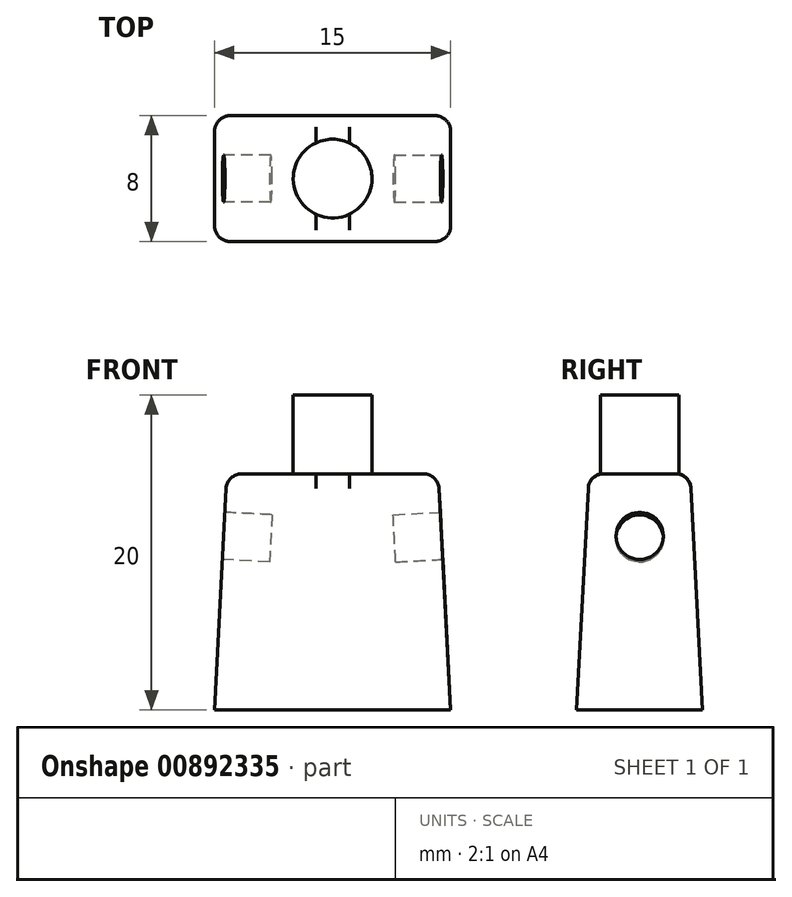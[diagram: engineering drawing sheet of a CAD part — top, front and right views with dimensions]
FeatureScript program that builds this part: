
annotation { "Feature Type Name" : "Feature", "Feature Type Description" : "" }
export const myFeature = defineFeature(function(context is Context, id is Id, definition is map)
    precondition{}
    {
        {
            var Q0;
            Q0=qCreatedBy(makeId("Top.planeOp"),FACE);
            var sketch = newSketch(context, id + "F0", { "sketchPlane" : qUnion([Q0])});
            skLineSegment(sketch, "E0.bottom", {"start": v(7.5, -4) * mm, "end": v(-7.5, -4) * mm});
            skLineSegment(sketch, "E0.top", {"start": v(7.5, 4) * mm, "end": v(-7.5, 4) * mm});
            skLineSegment(sketch, "E0.left", {"start": v(7.5, -4) * mm, "end": v(7.5, 4) * mm});
            skLineSegment(sketch, "E0.right", {"start": v(-7.5, -4) * mm, "end": v(-7.5, 4) * mm});
            skPoint(sketch, "E0.middle", {"position": v(0, 0) * mm});
            skSolve(sketch);
        }
        {
            var Q0;
            Q0 = qSketchRegion(id + "F0", true);
            extrude(context, id + "F1", {"entities" : qUnion([Q0]), "depth" : 15 * mm, "offsetDistance" : 25.4 * mm, "hasDraft" : true, "draftAngle" : 3 * degree, "draftPullDirection" : true});
        }
        {
            var Q0;
            Q0=makeQuery(id+"F1.opExtrude","CAP_FACE",FACE,{"disambiguationData":[OSD([sQuery(id+"F0.wireOp",EDGE,"E0.bottom"),sQuery(id+"F0.wireOp",EDGE,"E0.top"),sQuery(id+"F0.wireOp",EDGE,"E0.left"),sQuery(id+"F0.wireOp",EDGE,"E0.right")])],"isStart":false});
            var sketch = newSketch(context, id + "F2", { "sketchPlane" : qUnion([Q0])});
            skCircle(sketch, "E1", {"center": v(0, 0) * mm, "radius": 2.5 * mm});
            skSolve(sketch);
        }
        {
            var Q0;
            Q0 = qSketchRegion(id + "F2", true);
            extrude(context, id + "F3", {"entities" : qUnion([Q0]), "operationType" : NewBodyOperationType.ADD, "depth" : 5 * mm, "offsetDistance" : 25.4 * mm});
        }
        {
            var Q0;
            Q0=makeQuery(id+"F1.opExtrude","SWEPT_EDGE",EDGE,{"disambiguationData":[OSD([sQuery(id+"F0.wireOp",EDGE,"E0.bottom"),sQuery(id+"F0.wireOp",EDGE,"E0.left")])]});
            var Q1;
            Q1=makeQuery(id+"F1.opExtrude","SWEPT_EDGE",EDGE,{"disambiguationData":[OSD([sQuery(id+"F0.wireOp",EDGE,"E0.bottom"),sQuery(id+"F0.wireOp",EDGE,"E0.right")])]});
            var Q2;
            Q2=makeQuery(id+"F1.opExtrude","SWEPT_EDGE",EDGE,{"disambiguationData":[OSD([sQuery(id+"F0.wireOp",EDGE,"E0.top"),sQuery(id+"F0.wireOp",EDGE,"E0.left")])]});
            var Q3;
            Q3=makeQuery(id+"F1.opExtrude","CAP_EDGE",EDGE,{"disambiguationData":[OSD([sQuery(id+"F0.wireOp",EDGE,"E0.left")])],"isStart":false});
            var Q4;
            Q4=makeQuery(id+"F1.opExtrude","SWEPT_EDGE",EDGE,{"disambiguationData":[OSD([sQuery(id+"F0.wireOp",EDGE,"E0.top"),sQuery(id+"F0.wireOp",EDGE,"E0.right")])]});
            var Q5;
            Q5=makeQuery(id+"F1.opExtrude","CAP_EDGE",EDGE,{"disambiguationData":[OSD([sQuery(id+"F0.wireOp",EDGE,"E0.right")])],"isStart":false});
            var Q6;
            Q6=makeQuery(id+"F1.opExtrude","CAP_EDGE",EDGE,{"disambiguationData":[OSD([sQuery(id+"F0.wireOp",EDGE,"E0.top")])],"isStart":false});
            var Q7;
            Q7=makeQuery(id+"F1.opExtrude","CAP_EDGE",EDGE,{"disambiguationData":[OSD([sQuery(id+"F0.wireOp",EDGE,"E0.bottom")])],"isStart":false});
            fillet(context, id + "F4", {"entities" : qUnion([Q0, Q1, Q2, Q3, Q4, Q5, Q6, Q7]), "radius" : 1 * mm, "tangentPropagation" : true, "allowEdgeOverflow" : false});
        }
        {
            var Q0;
            Q0=makeQuery(id+"F1.opExtrude","SWEPT_FACE",FACE,{"disambiguationData":[OSD([sQuery(id+"F0.wireOp",EDGE,"E0.left")])]});
            var sketch = newSketch(context, id + "F5", { "sketchPlane" : qUnion([Q0])});
            skCircle(sketch, "E2", {"center": v(0, 10.68) * mm, "radius": 1.5 * mm});
            skSolve(sketch);
        }
        {
            var Q0;
            Q0=makeQuery(id+"F5.imprint","IMPRINT",FACE,{"disambiguationData":[TD([[makeQuery(id+"F5.imprint","IMPRINT",EDGE,{"derivedFrom":sQuery(id+"F5.wireOp",EDGE,"E2")}),1.0]])]});
            extrude(context, id + "F6", {"entities" : qUnion([Q0]), "operationType" : NewBodyOperationType.REMOVE, "oppositeDirection" : true, "depth" : 3 * mm, "offsetDistance" : 25.4 * mm});
        }
        {
            var Q0;
            Q0=makeQuery(id+"F1.opExtrude","SWEPT_FACE",FACE,{"disambiguationData":[OSD([sQuery(id+"F0.wireOp",EDGE,"E0.right")])]});
            var sketch = newSketch(context, id + "F7", { "sketchPlane" : qUnion([Q0])});
            skCircle(sketch, "E3", {"center": v(0, 10.68) * mm, "radius": 1.5 * mm});
            skSolve(sketch);
        }
        {
            var Q0;
            Q0 = qSketchRegion(id + "F7", true);
            extrude(context, id + "F8", {"entities" : qUnion([Q0]), "operationType" : NewBodyOperationType.REMOVE, "oppositeDirection" : true, "depth" : 3 * mm, "offsetDistance" : 25.4 * mm});
        }
    });
